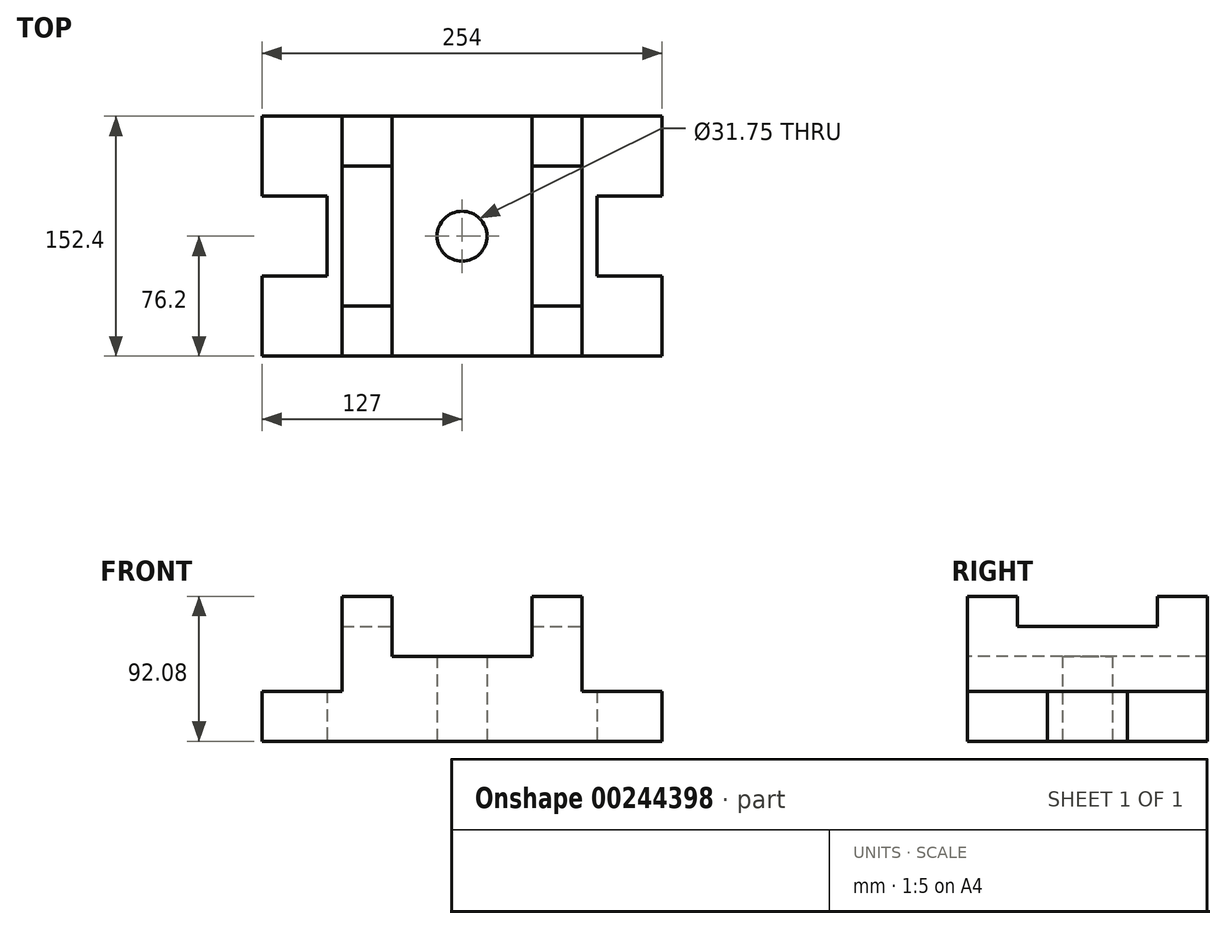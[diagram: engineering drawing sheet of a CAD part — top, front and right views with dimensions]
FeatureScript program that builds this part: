
annotation { "Feature Type Name" : "Feature", "Feature Type Description" : "" }
export const myFeature = defineFeature(function(context is Context, id is Id, definition is map)
    precondition{}
    {
        {
            var Q0;
            Q0=qCreatedBy(makeId("Top.planeOp"),FACE);
            var sketch = newSketch(context, id + "F0", { "sketchPlane" : qUnion([Q0])});
            skLineSegment(sketch, "E0.bottom", {"start": v(127, -76.2) * mm, "end": v(-127, -76.2) * mm});
            skLineSegment(sketch, "E0.top", {"start": v(127, 76.2) * mm, "end": v(-127, 76.2) * mm});
            skLineSegment(sketch, "E0.left", {"start": v(127, -76.2) * mm, "end": v(127, -25.4) * mm});
            skLineSegment(sketch, "E0.right", {"start": v(-127, -76.2) * mm, "end": v(-127, -25.4) * mm});
            skPoint(sketch, "E0.middle", {"position": v(0, 0) * mm});
            skLineSegment(sketch, "E1", {"start": v(-127, -25.4) * mm, "end": v(-85.72, -25.4) * mm});
            skLineSegment(sketch, "E2", {"start": v(-127, 25.4) * mm, "end": v(-85.72, 25.4) * mm});
            skLineSegment(sketch, "E3", {"start": v(-85.72, 25.4) * mm, "end": v(-85.72, -25.4) * mm});
            skLineSegment(sketch, "E4.trimOffspring", {"start": v(-127, 25.4) * mm, "end": v(-127, 76.2) * mm});
            skCircle(sketch, "E5", {"center": v(0, 0) * mm, "radius": 15.88 * mm});
            skLineSegment(sketch, "E6", {"start": v(-76.2, 76.2) * mm, "end": v(-76.2, -76.2) * mm});
            skLineSegment(sketch, "E7", {"start": v(-44.45, 76.2) * mm, "end": v(-44.45, -76.2) * mm});
            skLineSegment(sketch, "E8", {"start": v(-76.2, 44.45) * mm, "end": v(-44.45, 44.45) * mm});
            skLineSegment(sketch, "E9", {"start": v(-76.2, -44.45) * mm, "end": v(-44.45, -44.45) * mm});
            skLineSegment(sketch, "E10", {"start": v(127, 25.4) * mm, "end": v(85.72, 25.4) * mm});
            skLineSegment(sketch, "E11", {"start": v(127, -25.4) * mm, "end": v(85.72, -25.4) * mm});
            skLineSegment(sketch, "E12", {"start": v(85.72, 25.4) * mm, "end": v(85.72, -25.4) * mm});
            skLineSegment(sketch, "E13.trimOffspring", {"start": v(127, 25.4) * mm, "end": v(127, 76.2) * mm});
            skLineSegment(sketch, "E14", {"start": v(76.2, 76.2) * mm, "end": v(76.2, -76.2) * mm});
            skLineSegment(sketch, "E15", {"start": v(44.45, 76.2) * mm, "end": v(44.45, -76.2) * mm});
            skLineSegment(sketch, "E16", {"start": v(44.45, 44.45) * mm, "end": v(76.2, 44.45) * mm});
            skLineSegment(sketch, "E17", {"start": v(44.45, -44.45) * mm, "end": v(76.2, -44.45) * mm});
            skSolve(sketch);
        }
        {
            var Q0;
            {var subQ0=sQuery(id+"F0.wireOp",EDGE,"E0.right");Q0=makeQuery(id+"F0.imprint","IMPRINT",FACE,{"disambiguationData":[TD([[makeQuery(id+"F0.imprint","IMPRINT",EDGE,{"derivedFrom":subQ0}),-1.0]])]});}
            var Q1;
            {var subQ0=sQuery(id+"F0.wireOp",EDGE,"E0.left");Q1=makeQuery(id+"F0.imprint","IMPRINT",FACE,{"disambiguationData":[TD([[makeQuery(id+"F0.imprint","IMPRINT",EDGE,{"derivedFrom":subQ0}),1.0]])]});}
            extrude(context, id + "F1", {"entities" : qUnion([Q0, Q1]), "depth" : 31.75 * mm});
        }
        {
            var Q0;
            {var subQ5=sQuery(id+"F0.wireOp",EDGE,"E8");Q0=makeQuery(id+"F0.imprint","IMPRINT",FACE,{"disambiguationData":[TD([[makeQuery(id+"F0.imprint","IMPRINT",EDGE,{"derivedFrom":subQ5}),1.0]])]});}
            var Q1;
            {var subQ5=sQuery(id+"F0.wireOp",EDGE,"E9");Q1=makeQuery(id+"F0.imprint","IMPRINT",FACE,{"disambiguationData":[TD([[makeQuery(id+"F0.imprint","IMPRINT",EDGE,{"derivedFrom":subQ5}),-1.0]])]});}
            var Q2;
            {var subQ5=sQuery(id+"F0.wireOp",EDGE,"E17");Q2=makeQuery(id+"F0.imprint","IMPRINT",FACE,{"disambiguationData":[TD([[makeQuery(id+"F0.imprint","IMPRINT",EDGE,{"derivedFrom":subQ5}),-1.0]])]});}
            var Q3;
            {var subQ5=sQuery(id+"F0.wireOp",EDGE,"E16");Q3=makeQuery(id+"F0.imprint","IMPRINT",FACE,{"disambiguationData":[TD([[makeQuery(id+"F0.imprint","IMPRINT",EDGE,{"derivedFrom":subQ5}),1.0]])]});}
            extrude(context, id + "F2", {"entities" : qUnion([Q0, Q1, Q2, Q3]), "operationType" : NewBodyOperationType.ADD, "depth" : 92.07 * mm});
        }
        {
            var Q0;
            {var subQ0=sQuery(id+"F0.wireOp",EDGE,"E8");Q0=makeQuery(id+"F0.imprint","IMPRINT",FACE,{"disambiguationData":[TD([[makeQuery(id+"F0.imprint","IMPRINT",EDGE,{"derivedFrom":subQ0}),-1.0]])]});}
            var Q1;
            {var subQ0=sQuery(id+"F0.wireOp",EDGE,"E16");Q1=makeQuery(id+"F0.imprint","IMPRINT",FACE,{"disambiguationData":[TD([[makeQuery(id+"F0.imprint","IMPRINT",EDGE,{"derivedFrom":subQ0}),-1.0]])]});}
            extrude(context, id + "F3", {"entities" : qUnion([Q0, Q1]), "operationType" : NewBodyOperationType.ADD, "depth" : 73.02 * mm});
        }
        {
            var Q0;
            Q0=makeQuery(id+"F0.imprint","IMPRINT",FACE,{"disambiguationData":[TD([[makeQuery(id+"F0.imprint","IMPRINT",EDGE,{"derivedFrom":sQuery(id+"F0.wireOp",EDGE,"E5")}),-1.0]])]});
            extrude(context, id + "F4", {"entities" : qUnion([Q0]), "operationType" : NewBodyOperationType.ADD, "depth" : 53.97 * mm});
        }
    });
